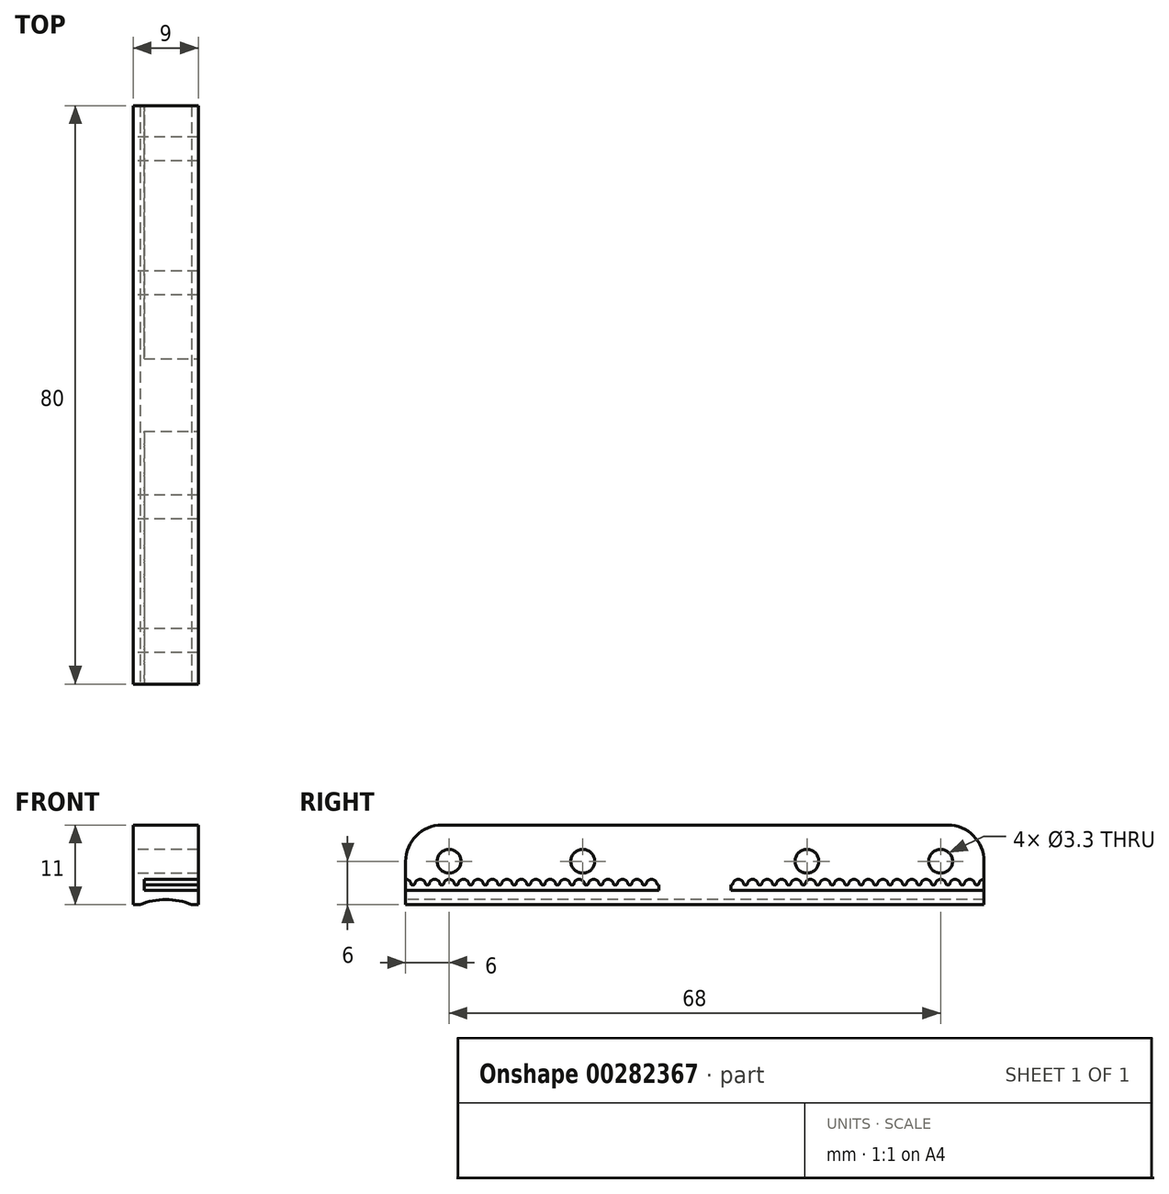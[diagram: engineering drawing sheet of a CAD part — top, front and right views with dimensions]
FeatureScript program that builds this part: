
annotation { "Feature Type Name" : "Feature", "Feature Type Description" : "" }
export const myFeature = defineFeature(function(context is Context, id is Id, definition is map)
    precondition{}
    {
        {
            var Q0;
            Q0=qCreatedBy(makeId("Right.planeOp"),FACE);
            var sketch = newSketch(context, id + "F0", { "sketchPlane" : qUnion([Q0])});
            skLineSegment(sketch, "E0.bottom", {"start": v(0, 0) * mm, "end": v(80, 0) * mm});
            skLineSegment(sketch, "E0.top", {"start": v(0, 11) * mm, "end": v(80, 11) * mm});
            skLineSegment(sketch, "E0.left", {"start": v(0, 0) * mm, "end": v(0, 11) * mm});
            skLineSegment(sketch, "E0.right", {"start": v(80, 0) * mm, "end": v(80, 11) * mm});
            skLineSegment(sketch, "E1", {"start": v(0, 6) * mm, "end": v(80, 6) * mm, "construction": true});
            skLineSegment(sketch, "E2", {"start": v(40, 6) * mm, "end": v(40, 0) * mm, "construction": true});
            skCircle(sketch, "E3", {"center": v(24.5, 6) * mm, "radius": 1.65 * mm});
            skCircle(sketch, "E4", {"center": v(6, 6) * mm, "radius": 1.65 * mm});
            skCircle(sketch, "E5", {"center": v(55.5, 6) * mm, "radius": 1.65 * mm});
            skCircle(sketch, "E6", {"center": v(74, 6) * mm, "radius": 1.65 * mm});
            skSolve(sketch);
        }
        {
            var Q0;
            Q0 = qSketchRegion(id + "F0", true);
            extrude(context, id + "F1", {"entities" : qUnion([Q0]), "depth" : 9 * mm});
        }
        {
            var Q0;
            Q0=makeQuery(id+"F1.opExtrude","CAP_FACE",FACE,{"disambiguationData":[OSD([sQuery(id+"F0.wireOp",EDGE,"E0.bottom"),sQuery(id+"F0.wireOp",EDGE,"E0.top"),sQuery(id+"F0.wireOp",EDGE,"E0.left"),sQuery(id+"F0.wireOp",EDGE,"E0.right"),sQuery(id+"F0.wireOp",EDGE,"E3"),sQuery(id+"F0.wireOp",EDGE,"E4"),sQuery(id+"F0.wireOp",EDGE,"E5"),sQuery(id+"F0.wireOp",EDGE,"E6")])],"isStart":false});
            var sketch = newSketch(context, id + "F2", { "sketchPlane" : qUnion([Q0])});
            skLineSegment(sketch, "E7", {"start": v(0, 2) * mm, "end": v(80, 2) * mm});
            skLineSegment(sketch, "E8", {"start": v(40, 11) * mm, "end": v(40, 0) * mm, "construction": true});
            skLineSegment(sketch, "E9.0", {"start": v(45, 10) * mm, "end": v(45, 0) * mm});
            skLineSegment(sketch, "E10", {"start": v(0, 2.75) * mm, "end": v(45, 2.75) * mm, "construction": true});
            skLineSegment(sketch, "E11", {"start": v(0, 3.5) * mm, "end": v(80, 3.5) * mm, "construction": true});
            skLineSegment(sketch, "E12.0", {"start": v(47, 10) * mm, "end": v(47, 0) * mm, "construction": true});
            skLineSegment(sketch, "E13.0", {"start": v(49, 10) * mm, "end": v(49, 0) * mm, "construction": true});
            skLineSegment(sketch, "E14", {"start": v(46, 3.5) * mm, "end": v(46, 2) * mm, "construction": true});
            skLineSegment(sketch, "E15", {"start": v(48, 3.5) * mm, "end": v(48, 2) * mm, "construction": true});
            skArc(sketch, "E16", {"start": v(46.74, 2.88) * mm, "mid": v(46, 3.5) * mm, "end": v(45.26, 2.88) * mm});
            skArc(sketch, "E17", {"start": v(48.74, 2.88) * mm, "mid": v(48, 3.5) * mm, "end": v(47.26, 2.88) * mm});
            skLineSegment(sketch, "E18.trimOffspring", {"start": v(45.25, 2.75) * mm, "end": v(46.75, 2.75) * mm, "construction": true});
            skLineSegment(sketch, "E19.trimOffspring", {"start": v(47.25, 2.75) * mm, "end": v(48.75, 2.75) * mm, "construction": true});
            skLineSegment(sketch, "E20", {"start": v(48.89, 2.75) * mm, "end": v(49, 2.75) * mm});
            skLineSegment(sketch, "E21", {"start": v(45, 2.75) * mm, "end": v(45.11, 2.75) * mm});
            skLineSegment(sketch, "E22", {"start": v(46.89, 2.75) * mm, "end": v(47.11, 2.75) * mm});
            skPoint(sketch, "E23.visualSharp", {"position": v(45.25, 2.75) * mm});
            skArc(sketch, "E23.filletArc", {"start": v(45.11, 2.75) * mm, "mid": v(45.2, 2.79) * mm, "end": v(45.26, 2.88) * mm});
            skPoint(sketch, "E24.visualSharp", {"position": v(46.75, 2.75) * mm});
            skArc(sketch, "E24.filletArc", {"start": v(46.74, 2.87) * mm, "mid": v(46.8, 2.79) * mm, "end": v(46.89, 2.75) * mm});
            skPoint(sketch, "E25.visualSharp", {"position": v(47.25, 2.75) * mm});
            skArc(sketch, "E25.filletArc", {"start": v(47.11, 2.75) * mm, "mid": v(47.2, 2.79) * mm, "end": v(47.26, 2.87) * mm});
            skPoint(sketch, "E26.visualSharp", {"position": v(48.75, 2.75) * mm});
            skArc(sketch, "E26.filletArc", {"start": v(48.74, 2.88) * mm, "mid": v(48.8, 2.79) * mm, "end": v(48.89, 2.75) * mm});
            skLineSegment(sketch, "E27.1.0.0", {"start": v(49, 2.75) * mm, "end": v(49.11, 2.75) * mm});
            skArc(sketch, "E27.1.0.1", {"start": v(49.11, 2.75) * mm, "mid": v(49.2, 2.79) * mm, "end": v(49.26, 2.88) * mm});
            skArc(sketch, "E27.1.0.2", {"start": v(50.74, 2.88) * mm, "mid": v(50, 3.5) * mm, "end": v(49.26, 2.88) * mm});
            skArc(sketch, "E27.1.0.3", {"start": v(50.74, 2.88) * mm, "mid": v(50.8, 2.79) * mm, "end": v(50.89, 2.75) * mm});
            skLineSegment(sketch, "E27.1.0.4", {"start": v(50.89, 2.75) * mm, "end": v(51.11, 2.75) * mm});
            skArc(sketch, "E27.1.0.5", {"start": v(51.11, 2.75) * mm, "mid": v(51.2, 2.79) * mm, "end": v(51.26, 2.87) * mm});
            skArc(sketch, "E27.1.0.6", {"start": v(52.74, 2.88) * mm, "mid": v(52, 3.5) * mm, "end": v(51.26, 2.88) * mm});
            skArc(sketch, "E27.1.0.7", {"start": v(52.74, 2.88) * mm, "mid": v(52.8, 2.79) * mm, "end": v(52.89, 2.75) * mm});
            skLineSegment(sketch, "E27.1.0.8", {"start": v(52.89, 2.75) * mm, "end": v(53, 2.75) * mm});
            skLineSegment(sketch, "E27.2.0.0", {"start": v(53, 2.75) * mm, "end": v(53.11, 2.75) * mm});
            skArc(sketch, "E27.2.0.1", {"start": v(53.11, 2.75) * mm, "mid": v(53.2, 2.79) * mm, "end": v(53.26, 2.88) * mm});
            skArc(sketch, "E27.2.0.2", {"start": v(54.74, 2.88) * mm, "mid": v(54, 3.5) * mm, "end": v(53.26, 2.88) * mm});
            skArc(sketch, "E27.2.0.3", {"start": v(54.74, 2.88) * mm, "mid": v(54.8, 2.79) * mm, "end": v(54.89, 2.75) * mm});
            skLineSegment(sketch, "E27.2.0.4", {"start": v(54.89, 2.75) * mm, "end": v(55.11, 2.75) * mm});
            skArc(sketch, "E27.2.0.5", {"start": v(55.11, 2.75) * mm, "mid": v(55.2, 2.79) * mm, "end": v(55.26, 2.88) * mm});
            skArc(sketch, "E27.2.0.6", {"start": v(56.74, 2.88) * mm, "mid": v(56, 3.5) * mm, "end": v(55.26, 2.88) * mm});
            skArc(sketch, "E27.2.0.7", {"start": v(56.74, 2.88) * mm, "mid": v(56.8, 2.79) * mm, "end": v(56.89, 2.75) * mm});
            skLineSegment(sketch, "E27.2.0.8", {"start": v(56.89, 2.75) * mm, "end": v(57, 2.75) * mm});
            skLineSegment(sketch, "E27.3.0.0", {"start": v(57, 2.75) * mm, "end": v(57.11, 2.75) * mm});
            skArc(sketch, "E27.3.0.1", {"start": v(57.11, 2.75) * mm, "mid": v(57.2, 2.79) * mm, "end": v(57.26, 2.88) * mm});
            skArc(sketch, "E27.3.0.2", {"start": v(58.74, 2.88) * mm, "mid": v(58, 3.5) * mm, "end": v(57.26, 2.88) * mm});
            skArc(sketch, "E27.3.0.3", {"start": v(58.74, 2.88) * mm, "mid": v(58.8, 2.79) * mm, "end": v(58.89, 2.75) * mm});
            skLineSegment(sketch, "E27.3.0.4", {"start": v(58.89, 2.75) * mm, "end": v(59.11, 2.75) * mm});
            skArc(sketch, "E27.3.0.5", {"start": v(59.11, 2.75) * mm, "mid": v(59.2, 2.79) * mm, "end": v(59.26, 2.88) * mm});
            skArc(sketch, "E27.3.0.6", {"start": v(60.74, 2.88) * mm, "mid": v(60, 3.5) * mm, "end": v(59.26, 2.88) * mm});
            skArc(sketch, "E27.3.0.7", {"start": v(60.74, 2.88) * mm, "mid": v(60.8, 2.79) * mm, "end": v(60.89, 2.75) * mm});
            skLineSegment(sketch, "E27.3.0.8", {"start": v(60.89, 2.75) * mm, "end": v(61, 2.75) * mm});
            skLineSegment(sketch, "E27.4.0.0", {"start": v(61, 2.75) * mm, "end": v(61.11, 2.75) * mm});
            skArc(sketch, "E27.4.0.1", {"start": v(61.11, 2.75) * mm, "mid": v(61.2, 2.79) * mm, "end": v(61.26, 2.88) * mm});
            skArc(sketch, "E27.4.0.2", {"start": v(62.74, 2.88) * mm, "mid": v(62, 3.5) * mm, "end": v(61.26, 2.88) * mm});
            skArc(sketch, "E27.4.0.3", {"start": v(62.74, 2.88) * mm, "mid": v(62.8, 2.79) * mm, "end": v(62.89, 2.75) * mm});
            skLineSegment(sketch, "E27.4.0.4", {"start": v(62.89, 2.75) * mm, "end": v(63.11, 2.75) * mm});
            skArc(sketch, "E27.4.0.5", {"start": v(63.11, 2.75) * mm, "mid": v(63.2, 2.79) * mm, "end": v(63.26, 2.88) * mm});
            skArc(sketch, "E27.4.0.6", {"start": v(64.74, 2.88) * mm, "mid": v(64, 3.5) * mm, "end": v(63.26, 2.88) * mm});
            skArc(sketch, "E27.4.0.7", {"start": v(64.74, 2.88) * mm, "mid": v(64.8, 2.79) * mm, "end": v(64.89, 2.75) * mm});
            skLineSegment(sketch, "E27.4.0.8", {"start": v(64.89, 2.75) * mm, "end": v(65, 2.75) * mm});
            skLineSegment(sketch, "E27.5.0.0", {"start": v(65, 2.75) * mm, "end": v(65.11, 2.75) * mm});
            skArc(sketch, "E27.5.0.1", {"start": v(65.11, 2.75) * mm, "mid": v(65.2, 2.79) * mm, "end": v(65.26, 2.88) * mm});
            skArc(sketch, "E27.5.0.2", {"start": v(66.74, 2.88) * mm, "mid": v(66, 3.5) * mm, "end": v(65.26, 2.88) * mm});
            skArc(sketch, "E27.5.0.3", {"start": v(66.74, 2.88) * mm, "mid": v(66.8, 2.79) * mm, "end": v(66.89, 2.75) * mm});
            skLineSegment(sketch, "E27.5.0.4", {"start": v(66.89, 2.75) * mm, "end": v(67.11, 2.75) * mm});
            skArc(sketch, "E27.5.0.5", {"start": v(67.11, 2.75) * mm, "mid": v(67.2, 2.79) * mm, "end": v(67.26, 2.88) * mm});
            skArc(sketch, "E27.5.0.6", {"start": v(68.74, 2.88) * mm, "mid": v(68, 3.5) * mm, "end": v(67.26, 2.88) * mm});
            skArc(sketch, "E27.5.0.7", {"start": v(68.74, 2.88) * mm, "mid": v(68.8, 2.79) * mm, "end": v(68.89, 2.75) * mm});
            skLineSegment(sketch, "E27.5.0.8", {"start": v(68.89, 2.75) * mm, "end": v(69, 2.75) * mm});
            skLineSegment(sketch, "E27.6.0.0", {"start": v(69, 2.75) * mm, "end": v(69.11, 2.75) * mm});
            skArc(sketch, "E27.6.0.1", {"start": v(69.11, 2.75) * mm, "mid": v(69.2, 2.79) * mm, "end": v(69.26, 2.88) * mm});
            skArc(sketch, "E27.6.0.2", {"start": v(70.74, 2.88) * mm, "mid": v(70, 3.5) * mm, "end": v(69.26, 2.88) * mm});
            skArc(sketch, "E27.6.0.3", {"start": v(70.74, 2.88) * mm, "mid": v(70.8, 2.79) * mm, "end": v(70.89, 2.75) * mm});
            skLineSegment(sketch, "E27.6.0.4", {"start": v(70.89, 2.75) * mm, "end": v(71.11, 2.75) * mm});
            skArc(sketch, "E27.6.0.5", {"start": v(71.11, 2.75) * mm, "mid": v(71.2, 2.79) * mm, "end": v(71.26, 2.88) * mm});
            skArc(sketch, "E27.6.0.6", {"start": v(72.74, 2.88) * mm, "mid": v(72, 3.5) * mm, "end": v(71.26, 2.88) * mm});
            skArc(sketch, "E27.6.0.7", {"start": v(72.74, 2.88) * mm, "mid": v(72.8, 2.79) * mm, "end": v(72.89, 2.75) * mm});
            skLineSegment(sketch, "E27.6.0.8", {"start": v(72.89, 2.75) * mm, "end": v(73, 2.75) * mm});
            skLineSegment(sketch, "E27.7.0.0", {"start": v(73, 2.75) * mm, "end": v(73.11, 2.75) * mm});
            skArc(sketch, "E27.7.0.1", {"start": v(73.11, 2.75) * mm, "mid": v(73.2, 2.79) * mm, "end": v(73.26, 2.88) * mm});
            skArc(sketch, "E27.7.0.2", {"start": v(74.74, 2.88) * mm, "mid": v(74, 3.5) * mm, "end": v(73.26, 2.88) * mm});
            skArc(sketch, "E27.7.0.3", {"start": v(74.74, 2.88) * mm, "mid": v(74.8, 2.79) * mm, "end": v(74.89, 2.75) * mm});
            skLineSegment(sketch, "E27.7.0.4", {"start": v(74.89, 2.75) * mm, "end": v(75.11, 2.75) * mm});
            skArc(sketch, "E27.7.0.5", {"start": v(75.11, 2.75) * mm, "mid": v(75.2, 2.79) * mm, "end": v(75.26, 2.88) * mm});
            skArc(sketch, "E27.7.0.6", {"start": v(76.74, 2.88) * mm, "mid": v(76, 3.5) * mm, "end": v(75.26, 2.88) * mm});
            skArc(sketch, "E27.7.0.7", {"start": v(76.74, 2.88) * mm, "mid": v(76.8, 2.79) * mm, "end": v(76.89, 2.75) * mm});
            skLineSegment(sketch, "E27.7.0.8", {"start": v(76.89, 2.75) * mm, "end": v(77, 2.75) * mm});
            skLineSegment(sketch, "E27.8.0.0", {"start": v(77, 2.75) * mm, "end": v(77.11, 2.75) * mm});
            skArc(sketch, "E27.8.0.1", {"start": v(77.11, 2.75) * mm, "mid": v(77.2, 2.79) * mm, "end": v(77.26, 2.88) * mm});
            skArc(sketch, "E27.8.0.2", {"start": v(78.74, 2.88) * mm, "mid": v(78, 3.5) * mm, "end": v(77.26, 2.88) * mm});
            skArc(sketch, "E27.8.0.3", {"start": v(78.74, 2.88) * mm, "mid": v(78.8, 2.79) * mm, "end": v(78.89, 2.75) * mm});
            skLineSegment(sketch, "E27.8.0.4", {"start": v(78.89, 2.75) * mm, "end": v(79.11, 2.75) * mm});
            skArc(sketch, "E27.8.0.5", {"start": v(79.11, 2.75) * mm, "mid": v(79.2, 2.79) * mm, "end": v(79.26, 2.88) * mm});
            skArc(sketch, "E27.8.0.6", {"start": v(80.74, 2.88) * mm, "mid": v(80, 3.5) * mm, "end": v(79.26, 2.88) * mm});
            skArc(sketch, "E27.8.0.7", {"start": v(80.74, 2.88) * mm, "mid": v(80.8, 2.79) * mm, "end": v(80.89, 2.75) * mm});
            skLineSegment(sketch, "E27.8.0.8", {"start": v(80.89, 2.75) * mm, "end": v(81, 2.75) * mm});
            skLineSegment(sketch, "E27.direction1", {"start": v(45, 2.75) * mm, "end": v(49, 2.75) * mm, "construction": true});
            skLineSegment(sketch, "E28", {"start": v(80, 2) * mm, "end": v(81, 2) * mm});
            skLineSegment(sketch, "E29", {"start": v(81, 2) * mm, "end": v(81, 2.75) * mm});
            skLineSegment(sketch, "E30.MirrorCS", {"start": v(35, 10) * mm, "end": v(35, 0) * mm});
            skArc(sketch, "E31.MirrorCS", {"start": v(34.89, 2.75) * mm, "mid": v(34.8, 2.79) * mm, "end": v(34.74, 2.88) * mm});
            skArc(sketch, "E32.MirrorCS", {"start": v(33.26, 2.87) * mm, "mid": v(34, 3.5) * mm, "end": v(34.74, 2.88) * mm});
            skArc(sketch, "E33.MirrorCS", {"start": v(33.26, 2.87) * mm, "mid": v(33.2, 2.79) * mm, "end": v(33.11, 2.75) * mm});
            skArc(sketch, "E34.MirrorCS", {"start": v(32.89, 2.75) * mm, "mid": v(32.8, 2.79) * mm, "end": v(32.74, 2.87) * mm});
            skArc(sketch, "E35.MirrorCS", {"start": v(31.26, 2.87) * mm, "mid": v(32, 3.5) * mm, "end": v(32.74, 2.87) * mm});
            skArc(sketch, "E36.MirrorCS", {"start": v(31.26, 2.87) * mm, "mid": v(31.2, 2.79) * mm, "end": v(31.11, 2.75) * mm});
            skLineSegment(sketch, "E37", {"start": v(34.89, 2.75) * mm, "end": v(35, 2.75) * mm});
            skLineSegment(sketch, "E38", {"start": v(33.11, 2.75) * mm, "end": v(32.89, 2.75) * mm});
            skLineSegment(sketch, "E39", {"start": v(31, 3.5) * mm, "end": v(31, 2) * mm, "construction": true});
            skArc(sketch, "E40.MirrorCS", {"start": v(30.89, 2.75) * mm, "mid": v(30.8, 2.79) * mm, "end": v(30.74, 2.88) * mm});
            skArc(sketch, "E41.MirrorCS", {"start": v(29.26, 2.87) * mm, "mid": v(30, 3.5) * mm, "end": v(30.74, 2.87) * mm});
            skArc(sketch, "E42.MirrorCS", {"start": v(29.26, 2.87) * mm, "mid": v(29.2, 2.79) * mm, "end": v(29.11, 2.75) * mm});
            skArc(sketch, "E43.MirrorCS", {"start": v(28.89, 2.75) * mm, "mid": v(28.8, 2.79) * mm, "end": v(28.74, 2.87) * mm});
            skArc(sketch, "E44.MirrorCS", {"start": v(27.26, 2.87) * mm, "mid": v(28, 3.5) * mm, "end": v(28.74, 2.87) * mm});
            skArc(sketch, "E45.MirrorCS", {"start": v(27.26, 2.87) * mm, "mid": v(27.2, 2.79) * mm, "end": v(27.11, 2.75) * mm});
            skArc(sketch, "E46.MirrorCS", {"start": v(26.89, 2.75) * mm, "mid": v(26.8, 2.79) * mm, "end": v(26.74, 2.88) * mm});
            skArc(sketch, "E47.MirrorCS", {"start": v(25.26, 2.87) * mm, "mid": v(26, 3.5) * mm, "end": v(26.74, 2.88) * mm});
            skArc(sketch, "E48.MirrorCS", {"start": v(25.26, 2.87) * mm, "mid": v(25.2, 2.79) * mm, "end": v(25.11, 2.75) * mm});
            skLineSegment(sketch, "E49.MirrorCS", {"start": v(25.11, 2.75) * mm, "end": v(24.89, 2.75) * mm});
            skLineSegment(sketch, "E50.MirrorCS", {"start": v(27, 2.75) * mm, "end": v(26.89, 2.75) * mm});
            skLineSegment(sketch, "E51.MirrorCS", {"start": v(27.11, 2.75) * mm, "end": v(27, 2.75) * mm});
            skLineSegment(sketch, "E52.MirrorCS", {"start": v(29.11, 2.75) * mm, "end": v(28.89, 2.75) * mm});
            skArc(sketch, "E53.MirrorCS", {"start": v(24.89, 2.75) * mm, "mid": v(24.8, 2.79) * mm, "end": v(24.74, 2.87) * mm});
            skArc(sketch, "E54.MirrorCS", {"start": v(23.26, 2.87) * mm, "mid": v(24, 3.5) * mm, "end": v(24.74, 2.87) * mm});
            skArc(sketch, "E55.MirrorCS", {"start": v(23.26, 2.87) * mm, "mid": v(23.2, 2.79) * mm, "end": v(23.11, 2.75) * mm});
            skLineSegment(sketch, "E56.MirrorCS", {"start": v(23.11, 2.75) * mm, "end": v(23, 2.75) * mm});
            skLineSegment(sketch, "E57.MirrorCS", {"start": v(23, 2.75) * mm, "end": v(22.89, 2.75) * mm});
            skArc(sketch, "E58.MirrorCS", {"start": v(22.89, 2.75) * mm, "mid": v(22.8, 2.79) * mm, "end": v(22.74, 2.88) * mm});
            skArc(sketch, "E59.MirrorCS", {"start": v(21.26, 2.87) * mm, "mid": v(22, 3.5) * mm, "end": v(22.74, 2.88) * mm});
            skArc(sketch, "E60.MirrorCS", {"start": v(21.26, 2.87) * mm, "mid": v(21.2, 2.79) * mm, "end": v(21.11, 2.75) * mm});
            skLineSegment(sketch, "E61.MirrorCS", {"start": v(21.11, 2.75) * mm, "end": v(20.89, 2.75) * mm});
            skArc(sketch, "E62.MirrorCS", {"start": v(20.89, 2.75) * mm, "mid": v(20.8, 2.79) * mm, "end": v(20.74, 2.87) * mm});
            skArc(sketch, "E63.MirrorCS", {"start": v(19.26, 2.87) * mm, "mid": v(20, 3.5) * mm, "end": v(20.74, 2.87) * mm});
            skArc(sketch, "E64.MirrorCS", {"start": v(19.26, 2.87) * mm, "mid": v(19.2, 2.79) * mm, "end": v(19.11, 2.75) * mm});
            skLineSegment(sketch, "E65.MirrorCS", {"start": v(19.11, 2.75) * mm, "end": v(19, 2.75) * mm});
            skLineSegment(sketch, "E66.MirrorCS", {"start": v(19, 2.75) * mm, "end": v(18.89, 2.75) * mm});
            skArc(sketch, "E67.MirrorCS", {"start": v(18.89, 2.75) * mm, "mid": v(18.8, 2.79) * mm, "end": v(18.74, 2.88) * mm});
            skArc(sketch, "E68.MirrorCS", {"start": v(17.26, 2.88) * mm, "mid": v(18, 3.5) * mm, "end": v(18.74, 2.88) * mm});
            skArc(sketch, "E69.MirrorCS", {"start": v(17.26, 2.88) * mm, "mid": v(17.2, 2.79) * mm, "end": v(17.11, 2.75) * mm});
            skLineSegment(sketch, "E70.MirrorCS", {"start": v(17.11, 2.75) * mm, "end": v(16.89, 2.75) * mm});
            skArc(sketch, "E71.MirrorCS", {"start": v(16.89, 2.75) * mm, "mid": v(16.8, 2.79) * mm, "end": v(16.74, 2.87) * mm});
            skArc(sketch, "E72.MirrorCS", {"start": v(15.26, 2.88) * mm, "mid": v(16, 3.5) * mm, "end": v(16.74, 2.88) * mm});
            skArc(sketch, "E73.MirrorCS", {"start": v(15.26, 2.87) * mm, "mid": v(15.2, 2.79) * mm, "end": v(15.11, 2.75) * mm});
            skLineSegment(sketch, "E74.MirrorCS", {"start": v(15.11, 2.75) * mm, "end": v(15, 2.75) * mm});
            skLineSegment(sketch, "E75.MirrorCS", {"start": v(15, 2.75) * mm, "end": v(14.89, 2.75) * mm});
            skArc(sketch, "E76.MirrorCS", {"start": v(14.89, 2.75) * mm, "mid": v(14.8, 2.79) * mm, "end": v(14.74, 2.88) * mm});
            skArc(sketch, "E77.MirrorCS", {"start": v(13.26, 2.87) * mm, "mid": v(14, 3.5) * mm, "end": v(14.74, 2.88) * mm});
            skArc(sketch, "E78.MirrorCS", {"start": v(13.26, 2.87) * mm, "mid": v(13.2, 2.79) * mm, "end": v(13.11, 2.75) * mm});
            skLineSegment(sketch, "E79.MirrorCS", {"start": v(13.11, 2.75) * mm, "end": v(12.89, 2.75) * mm});
            skArc(sketch, "E80.MirrorCS", {"start": v(12.89, 2.75) * mm, "mid": v(12.8, 2.79) * mm, "end": v(12.74, 2.88) * mm});
            skArc(sketch, "E81.MirrorCS", {"start": v(11.26, 2.87) * mm, "mid": v(12, 3.5) * mm, "end": v(12.74, 2.88) * mm});
            skArc(sketch, "E82.MirrorCS", {"start": v(11.26, 2.87) * mm, "mid": v(11.2, 2.79) * mm, "end": v(11.11, 2.75) * mm});
            skLineSegment(sketch, "E83.MirrorCS", {"start": v(11.11, 2.75) * mm, "end": v(11, 2.75) * mm});
            skLineSegment(sketch, "E84.MirrorCS", {"start": v(11, 2.75) * mm, "end": v(10.89, 2.75) * mm});
            skArc(sketch, "E85.MirrorCS", {"start": v(10.89, 2.75) * mm, "mid": v(10.8, 2.79) * mm, "end": v(10.74, 2.88) * mm});
            skArc(sketch, "E86.MirrorCS", {"start": v(9.26, 2.87) * mm, "mid": v(10, 3.5) * mm, "end": v(10.74, 2.88) * mm});
            skArc(sketch, "E87.MirrorCS", {"start": v(9.26, 2.88) * mm, "mid": v(9.2, 2.79) * mm, "end": v(9.11, 2.75) * mm});
            skLineSegment(sketch, "E88.MirrorCS", {"start": v(9.11, 2.75) * mm, "end": v(8.89, 2.75) * mm});
            skArc(sketch, "E89.MirrorCS", {"start": v(8.89, 2.75) * mm, "mid": v(8.8, 2.79) * mm, "end": v(8.74, 2.88) * mm});
            skArc(sketch, "E90.MirrorCS", {"start": v(7.26, 2.88) * mm, "mid": v(8, 3.5) * mm, "end": v(8.74, 2.88) * mm});
            skArc(sketch, "E91.MirrorCS", {"start": v(7.26, 2.88) * mm, "mid": v(7.2, 2.79) * mm, "end": v(7.11, 2.75) * mm});
            skLineSegment(sketch, "E92.MirrorCS", {"start": v(7.11, 2.75) * mm, "end": v(7, 2.75) * mm});
            skLineSegment(sketch, "E93.MirrorCS", {"start": v(7, 2.75) * mm, "end": v(6.89, 2.75) * mm});
            skArc(sketch, "E94.MirrorCS", {"start": v(6.89, 2.75) * mm, "mid": v(6.8, 2.79) * mm, "end": v(6.74, 2.88) * mm});
            skArc(sketch, "E95.MirrorCS", {"start": v(5.26, 2.88) * mm, "mid": v(6, 3.5) * mm, "end": v(6.74, 2.88) * mm});
            skArc(sketch, "E96.MirrorCS", {"start": v(5.26, 2.88) * mm, "mid": v(5.2, 2.79) * mm, "end": v(5.11, 2.75) * mm});
            skLineSegment(sketch, "E97.MirrorCS", {"start": v(5.11, 2.75) * mm, "end": v(4.89, 2.75) * mm});
            skArc(sketch, "E98.MirrorCS", {"start": v(4.89, 2.75) * mm, "mid": v(4.8, 2.79) * mm, "end": v(4.74, 2.88) * mm});
            skArc(sketch, "E99.MirrorCS", {"start": v(3.26, 2.88) * mm, "mid": v(4, 3.5) * mm, "end": v(4.74, 2.87) * mm});
            skArc(sketch, "E100.MirrorCS", {"start": v(3.26, 2.88) * mm, "mid": v(3.2, 2.79) * mm, "end": v(3.11, 2.75) * mm});
            skLineSegment(sketch, "E101.MirrorCS", {"start": v(3.11, 2.75) * mm, "end": v(3, 2.75) * mm});
            skLineSegment(sketch, "E102.MirrorCS", {"start": v(3, 2.75) * mm, "end": v(2.89, 2.75) * mm});
            skArc(sketch, "E103.MirrorCS", {"start": v(2.89, 2.75) * mm, "mid": v(2.8, 2.79) * mm, "end": v(2.74, 2.88) * mm});
            skArc(sketch, "E104.MirrorCS", {"start": v(1.26, 2.88) * mm, "mid": v(2, 3.5) * mm, "end": v(2.74, 2.88) * mm});
            skArc(sketch, "E105.MirrorCS", {"start": v(1.26, 2.88) * mm, "mid": v(1.2, 2.79) * mm, "end": v(1.11, 2.75) * mm});
            skArc(sketch, "E106.MirrorCS", {"start": v(0.89, 2.75) * mm, "mid": v(0.8, 2.79) * mm, "end": v(0.74, 2.88) * mm});
            skArc(sketch, "E107.MirrorCS", {"start": v(-0.74, 2.88) * mm, "mid": v(0, 3.5) * mm, "end": v(0.74, 2.88) * mm});
            skArc(sketch, "E108.MirrorCS", {"start": v(-0.74, 2.88) * mm, "mid": v(-0.8, 2.79) * mm, "end": v(-0.89, 2.75) * mm});
            skLineSegment(sketch, "E109.MirrorCS", {"start": v(-0.89, 2.75) * mm, "end": v(-1, 2.75) * mm});
            skLineSegment(sketch, "E110.MirrorCS", {"start": v(-1, 2) * mm, "end": v(-1, 2.75) * mm});
            skLineSegment(sketch, "E111.MirrorCS", {"start": v(0, 2) * mm, "end": v(-1, 2) * mm});
            skLineSegment(sketch, "E112", {"start": v(30.89, 2.75) * mm, "end": v(31.11, 2.75) * mm});
            skLineSegment(sketch, "E113", {"start": v(0.89, 2.75) * mm, "end": v(1.11, 2.75) * mm});
            skSolve(sketch);
        }
        {
            var Q0;
            Q0 = qSketchRegion(id + "F2", true);
            extrude(context, id + "F3", {"entities" : qUnion([Q0]), "operationType" : NewBodyOperationType.REMOVE, "oppositeDirection" : true, "depth" : 7.5 * mm});
        }
        {
            var Q0;
            Q0=makeQuery(id+"F1.opExtrude","SWEPT_EDGE",EDGE,{"disambiguationData":[OSD([sQuery(id+"F0.wireOp",EDGE,"E0.top"),sQuery(id+"F0.wireOp",EDGE,"E0.left")])]});
            var Q1;
            Q1=makeQuery(id+"F1.opExtrude","SWEPT_EDGE",EDGE,{"disambiguationData":[OSD([sQuery(id+"F0.wireOp",EDGE,"E0.top"),sQuery(id+"F0.wireOp",EDGE,"E0.right")])]});
            fillet(context, id + "F4", {"entities" : qUnion([Q0, Q1]), "radius" : 5 * mm, "tangentPropagation" : true, "allowEdgeOverflow" : false});
        }
        {
            var Q0;
            Q0=qCreatedBy(makeId("Front.planeOp"),FACE);
            var sketch = newSketch(context, id + "F5", { "sketchPlane" : qUnion([Q0])});
            skLineSegment(sketch, "E114", {"start": v(0, 0) * mm, "end": v(4.5, 0) * mm, "construction": true});
            skLineSegment(sketch, "E115", {"start": v(4.5, 0) * mm, "end": v(4.5, -8.8) * mm, "construction": true});
            skCircle(sketch, "E116", {"center": v(4.5, -8.8) * mm, "radius": 9.5 * mm});
            skSolve(sketch);
        }
        {
            var Q0;
            Q0 = qSketchRegion(id + "F5", true);
            extrude(context, id + "F6", {"entities" : qUnion([Q0]), "operationType" : NewBodyOperationType.REMOVE, "endBound" : BoundingType.THROUGH_ALL, "oppositeDirection" : true, "depth" : 25 * mm});
        }
    });
